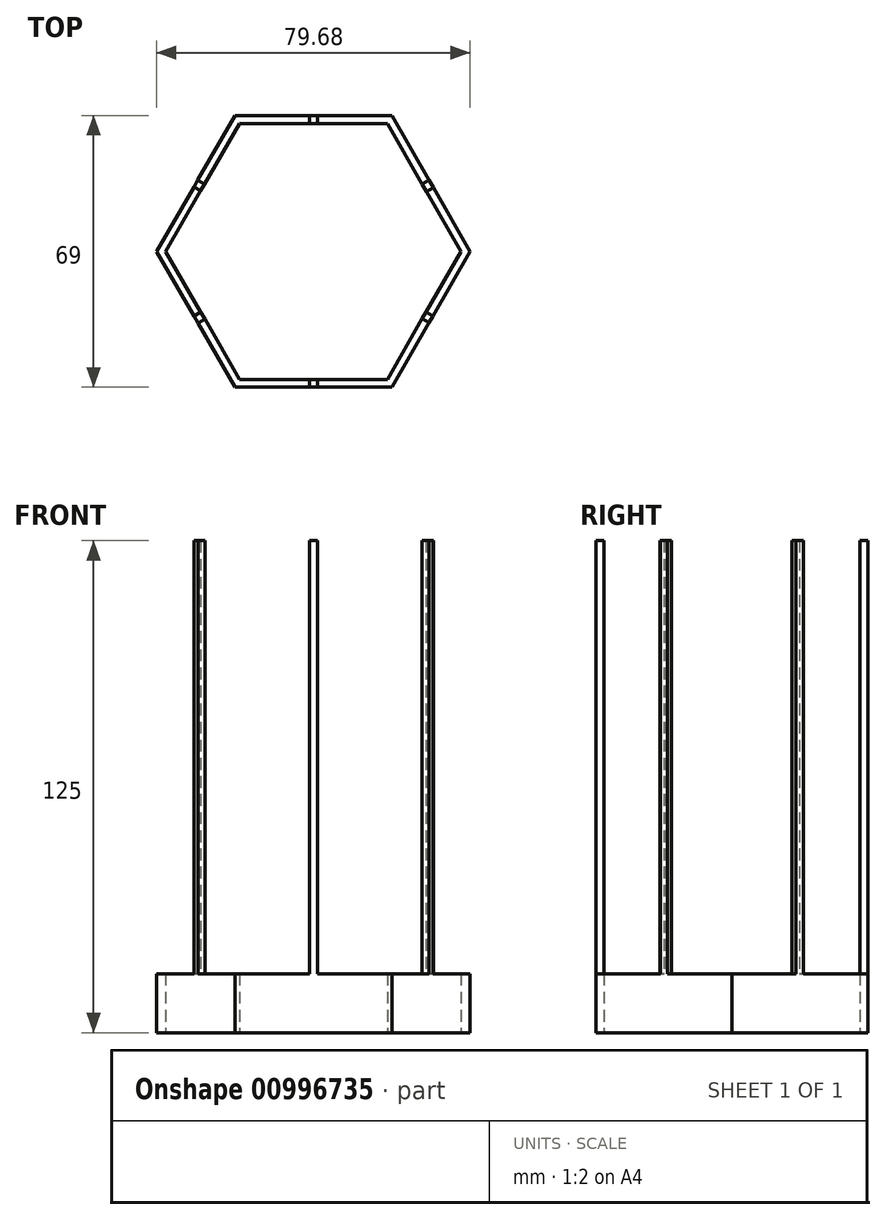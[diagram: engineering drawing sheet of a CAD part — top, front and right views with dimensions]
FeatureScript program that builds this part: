
annotation { "Feature Type Name" : "Feature", "Feature Type Description" : "" }
export const myFeature = defineFeature(function(context is Context, id is Id, definition is map)
    precondition{}
    {
        {
            var Q0;
            Q0=qCreatedBy(makeId("Top.planeOp"),FACE);
            var sketch = newSketch(context, id + "F0", { "sketchPlane" : qUnion([Q0])});
            skCircle(sketch, "E0.cCircle", {"center": v(0, 0) * mm, "radius": 34.5 * mm, "construction": true});
            skLineSegment(sketch, "E0.0", {"start": v(19.92, -34.5) * mm, "end": v(-19.92, -34.5) * mm});
            skLineSegment(sketch, "E0.1", {"start": v(-19.92, -34.5) * mm, "end": v(-39.84, 0) * mm});
            skLineSegment(sketch, "E0.2", {"start": v(-39.84, 0) * mm, "end": v(-19.92, 34.5) * mm});
            skLineSegment(sketch, "E0.3", {"start": v(-19.92, 34.5) * mm, "end": v(19.92, 34.5) * mm});
            skLineSegment(sketch, "E0.4", {"start": v(19.92, 34.5) * mm, "end": v(39.84, 0) * mm});
            skLineSegment(sketch, "E0.5", {"start": v(39.84, 0) * mm, "end": v(19.92, -34.5) * mm});
            skPoint(sketch, "E0.0.midPoint", {"position": v(0, -34.5) * mm});
            skCircle(sketch, "E1.cCircle", {"center": v(0, 0) * mm, "radius": 32.5 * mm, "construction": true});
            skLineSegment(sketch, "E1.0", {"start": v(18.76, -32.5) * mm, "end": v(-18.76, -32.5) * mm});
            skLineSegment(sketch, "E1.1", {"start": v(-18.76, -32.5) * mm, "end": v(-37.53, 0) * mm});
            skLineSegment(sketch, "E1.2", {"start": v(-37.53, 0) * mm, "end": v(-18.76, 32.5) * mm});
            skLineSegment(sketch, "E1.3", {"start": v(-18.76, 32.5) * mm, "end": v(18.76, 32.5) * mm});
            skLineSegment(sketch, "E1.4", {"start": v(18.76, 32.5) * mm, "end": v(37.53, 0) * mm});
            skLineSegment(sketch, "E1.5", {"start": v(37.53, 0) * mm, "end": v(18.76, -32.5) * mm});
            skPoint(sketch, "E1.0.midPoint", {"position": v(0, -32.5) * mm});
            skSolve(sketch);
        }
        {
            var Q0;
            Q0=makeQuery(id+"F0.imprint","IMPRINT",FACE,{"disambiguationData":[TD([[makeQuery(id+"F0.imprint","IMPRINT",EDGE,{"derivedFrom":sQuery(id+"F0.wireOp",EDGE,"E0.0")}),-1.0]])]});
            extrude(context, id + "F1", {"entities" : qUnion([Q0]), "depth" : 15 * mm, "offsetDistance" : 25 * mm});
        }
        {
            var Q0;
            Q0=makeQuery(id+"F1.opExtrude","CAP_FACE",FACE,{"disambiguationData":[OSD([sQuery(id+"F0.wireOp",EDGE,"E0.0"),sQuery(id+"F0.wireOp",EDGE,"E0.1"),sQuery(id+"F0.wireOp",EDGE,"E0.2"),sQuery(id+"F0.wireOp",EDGE,"E0.3"),sQuery(id+"F0.wireOp",EDGE,"E0.4"),sQuery(id+"F0.wireOp",EDGE,"E0.5"),sQuery(id+"F0.wireOp",EDGE,"E1.0"),sQuery(id+"F0.wireOp",EDGE,"E1.1"),sQuery(id+"F0.wireOp",EDGE,"E1.2"),sQuery(id+"F0.wireOp",EDGE,"E1.3"),sQuery(id+"F0.wireOp",EDGE,"E1.4"),sQuery(id+"F0.wireOp",EDGE,"E1.5")])],"isStart":false});
            var sketch = newSketch(context, id + "F2", { "sketchPlane" : qUnion([Q0])});
            skLineSegment(sketch, "E2", {"start": v(0, -34.5) * mm, "end": v(0, 34.5) * mm});
            skLineSegment(sketch, "E3", {"start": v(0, 34.5) * mm, "end": v(1, 34.5) * mm});
            skLineSegment(sketch, "E4", {"start": v(1, 34.5) * mm, "end": v(1, -34.5) * mm});
            skLineSegment(sketch, "E5", {"start": v(-1, -34.5) * mm, "end": v(-1, 34.5) * mm});
            skLineSegment(sketch, "E6", {"start": v(-29.88, 17.25) * mm, "end": v(29.88, -17.25) * mm});
            skLineSegment(sketch, "E7", {"start": v(-30.38, 16.38) * mm, "end": v(29.38, -18.12) * mm});
            skLineSegment(sketch, "E8", {"start": v(-29.38, 18.12) * mm, "end": v(30.38, -16.38) * mm});
            skLineSegment(sketch, "E9", {"start": v(29.88, 17.25) * mm, "end": v(-29.88, -17.25) * mm});
            skLineSegment(sketch, "E10", {"start": v(-30.38, -16.38) * mm, "end": v(29.38, 18.12) * mm});
            skLineSegment(sketch, "E11", {"start": v(30.46, 16.25) * mm, "end": v(-29.3, -18.25) * mm});
            skPoint(sketch, "E11.startSnap0", {"position": v(28.15, 16.25) * mm});
            skSolve(sketch);
        }
        {
            var Q0;
            {var subQ0=sQuery(id+"F2.wireOp",EDGE,"E6");var subQ1=makeQuery(id+"F1.opExtrude","CAP_EDGE",EDGE,{"disambiguationData":[OSD([sQuery(id+"F0.wireOp",EDGE,"E0.2")])],"isStart":false});var subQ2=makeQuery(id+"F2.imprint","INTERSECT",VERTEX,{"derivedFrom":[subQ1,subQ0]});Q0=makeQuery(id+"F2.imprint","IMPRINT",FACE,{"disambiguationData":[TD([[makeQuery(id+"F2.imprint","IMPRINT",EDGE,{"disambiguationData":[TD([[subQ2,-1.0]])],"derivedFrom":subQ0}),-1.0]])]});}
            var Q1;
            {var subQ0=sQuery(id+"F2.wireOp",EDGE,"E6");var subQ1=makeQuery(id+"F1.opExtrude","CAP_EDGE",EDGE,{"disambiguationData":[OSD([sQuery(id+"F0.wireOp",EDGE,"E0.2")])],"isStart":false});var subQ2=makeQuery(id+"F2.imprint","INTERSECT",VERTEX,{"derivedFrom":[subQ1,subQ0]});Q1=makeQuery(id+"F2.imprint","IMPRINT",FACE,{"disambiguationData":[TD([[makeQuery(id+"F2.imprint","IMPRINT",EDGE,{"disambiguationData":[TD([[subQ2,-1.0]])],"derivedFrom":subQ0}),1.0]])]});}
            var Q2;
            {var subQ1=makeQuery(id+"F1.opExtrude","CAP_EDGE",EDGE,{"disambiguationData":[OSD([sQuery(id+"F0.wireOp",EDGE,"E0.3")])],"isStart":false});var subQ5=sQuery(id+"F2.wireOp",EDGE,"E5");var subQ6=makeQuery(id+"F2.imprint","INTERSECT",VERTEX,{"derivedFrom":[subQ1,subQ5]});Q2=makeQuery(id+"F2.imprint","IMPRINT",FACE,{"disambiguationData":[TD([[makeQuery(id+"F2.imprint","IMPRINT",EDGE,{"disambiguationData":[TD([[subQ6,1.0]])],"derivedFrom":subQ5}),-1.0]])]});}
            var Q3;
            {var subQ0=sQuery(id+"F2.wireOp",EDGE,"E3");Q3=makeQuery(id+"F2.imprint","IMPRINT",FACE,{"disambiguationData":[TD([[makeQuery(id+"F2.imprint","IMPRINT",EDGE,{"derivedFrom":subQ0}),-1.0]])]});}
            var Q4;
            {var subQ0=sQuery(id+"F2.wireOp",EDGE,"E9");var subQ1=makeQuery(id+"F1.opExtrude","CAP_EDGE",EDGE,{"disambiguationData":[OSD([sQuery(id+"F0.wireOp",EDGE,"E0.4")])],"isStart":false});var subQ2=makeQuery(id+"F2.imprint","INTERSECT",VERTEX,{"derivedFrom":[subQ1,subQ0]});Q4=makeQuery(id+"F2.imprint","IMPRINT",FACE,{"disambiguationData":[TD([[makeQuery(id+"F2.imprint","IMPRINT",EDGE,{"disambiguationData":[TD([[subQ2,-1.0]])],"derivedFrom":subQ0}),-1.0]])]});}
            var Q5;
            {var subQ0=sQuery(id+"F2.wireOp",EDGE,"E9");var subQ1=makeQuery(id+"F1.opExtrude","CAP_EDGE",EDGE,{"disambiguationData":[OSD([sQuery(id+"F0.wireOp",EDGE,"E0.4")])],"isStart":false});var subQ2=makeQuery(id+"F2.imprint","INTERSECT",VERTEX,{"derivedFrom":[subQ1,subQ0]});Q5=makeQuery(id+"F2.imprint","IMPRINT",FACE,{"disambiguationData":[TD([[makeQuery(id+"F2.imprint","IMPRINT",EDGE,{"disambiguationData":[TD([[subQ2,-1.0]])],"derivedFrom":subQ0}),1.0]])]});}
            var Q6;
            {var subQ0=sQuery(id+"F2.wireOp",EDGE,"E6");var subQ1=makeQuery(id+"F1.opExtrude","CAP_EDGE",EDGE,{"disambiguationData":[OSD([sQuery(id+"F0.wireOp",EDGE,"E0.5")])],"isStart":false});var subQ2=makeQuery(id+"F2.imprint","INTERSECT",VERTEX,{"derivedFrom":[subQ1,subQ0]});Q6=makeQuery(id+"F2.imprint","IMPRINT",FACE,{"disambiguationData":[TD([[makeQuery(id+"F2.imprint","IMPRINT",EDGE,{"disambiguationData":[TD([[subQ2,1.0]])],"derivedFrom":subQ0}),1.0]])]});}
            var Q7;
            {var subQ0=sQuery(id+"F2.wireOp",EDGE,"E6");var subQ1=makeQuery(id+"F1.opExtrude","CAP_EDGE",EDGE,{"disambiguationData":[OSD([sQuery(id+"F0.wireOp",EDGE,"E0.5")])],"isStart":false});var subQ2=makeQuery(id+"F2.imprint","INTERSECT",VERTEX,{"derivedFrom":[subQ1,subQ0]});Q7=makeQuery(id+"F2.imprint","IMPRINT",FACE,{"disambiguationData":[TD([[makeQuery(id+"F2.imprint","IMPRINT",EDGE,{"disambiguationData":[TD([[subQ2,1.0]])],"derivedFrom":subQ0}),-1.0]])]});}
            var Q8;
            {var subQ0=sQuery(id+"F2.wireOp",EDGE,"E2");var subQ1=makeQuery(id+"F1.opExtrude","CAP_EDGE",EDGE,{"disambiguationData":[OSD([sQuery(id+"F0.wireOp",EDGE,"E0.0")])],"isStart":false});var subQ2=makeQuery(id+"F2.imprint","INTERSECT",VERTEX,{"derivedFrom":[subQ1,subQ0]});Q8=makeQuery(id+"F2.imprint","IMPRINT",FACE,{"disambiguationData":[TD([[makeQuery(id+"F2.imprint","IMPRINT",EDGE,{"disambiguationData":[TD([[subQ2,-1.0]])],"derivedFrom":subQ0}),-1.0]])]});}
            var Q9;
            {var subQ0=sQuery(id+"F2.wireOp",EDGE,"E2");var subQ1=makeQuery(id+"F1.opExtrude","CAP_EDGE",EDGE,{"disambiguationData":[OSD([sQuery(id+"F0.wireOp",EDGE,"E0.0")])],"isStart":false});var subQ2=makeQuery(id+"F2.imprint","INTERSECT",VERTEX,{"derivedFrom":[subQ1,subQ0]});Q9=makeQuery(id+"F2.imprint","IMPRINT",FACE,{"disambiguationData":[TD([[makeQuery(id+"F2.imprint","IMPRINT",EDGE,{"disambiguationData":[TD([[subQ2,-1.0]])],"derivedFrom":subQ0}),1.0]])]});}
            var Q10;
            {var subQ0=sQuery(id+"F2.wireOp",EDGE,"E9");var subQ1=makeQuery(id+"F1.opExtrude","CAP_EDGE",EDGE,{"disambiguationData":[OSD([sQuery(id+"F0.wireOp",EDGE,"E0.1")])],"isStart":false});var subQ2=makeQuery(id+"F2.imprint","INTERSECT",VERTEX,{"derivedFrom":[subQ1,subQ0]});Q10=makeQuery(id+"F2.imprint","IMPRINT",FACE,{"disambiguationData":[TD([[makeQuery(id+"F2.imprint","IMPRINT",EDGE,{"disambiguationData":[TD([[subQ2,1.0]])],"derivedFrom":subQ0}),1.0]])]});}
            var Q11;
            {var subQ0=sQuery(id+"F2.wireOp",EDGE,"E9");var subQ1=makeQuery(id+"F1.opExtrude","CAP_EDGE",EDGE,{"disambiguationData":[OSD([sQuery(id+"F0.wireOp",EDGE,"E0.1")])],"isStart":false});var subQ2=makeQuery(id+"F2.imprint","INTERSECT",VERTEX,{"derivedFrom":[subQ1,subQ0]});Q11=makeQuery(id+"F2.imprint","IMPRINT",FACE,{"disambiguationData":[TD([[makeQuery(id+"F2.imprint","IMPRINT",EDGE,{"disambiguationData":[TD([[subQ2,1.0]])],"derivedFrom":subQ0}),-1.0]])]});}
            extrude(context, id + "F3", {"entities" : qUnion([Q0, Q1, Q2, Q3, Q4, Q5, Q6, Q7, Q8, Q9, Q10, Q11]), "operationType" : NewBodyOperationType.ADD, "depth" : 110 * mm, "offsetDistance" : 25 * mm});
        }
        {
            var Q0;
            {var subQ0=sQuery(id+"F0.wireOp",EDGE,"E0.3");Q0=makeQuery(id+"F3.boolean.opBoolean","MERGE",FACE,{"derivedFrom":[makeQuery(id+"F1.opExtrude","SWEPT_FACE",FACE,{"disambiguationData":[OSD([subQ0])]}),makeQuery(id+"F3.opExtrude","SWEPT_FACE",FACE,{"disambiguationData":[OSD([subQ0,sQuery(id+"F2.wireOp",EDGE,"E3")])]})]});}
            var sketch = newSketch(context, id + "F4", { "sketchPlane" : qUnion([Q0])});
            skLineSegment(sketch, "E12.bottom", {"start": v(-1, 37) * mm, "end": v(1, 37) * mm});
            skLineSegment(sketch, "E12.top", {"start": v(-1, 35) * mm, "end": v(1, 35) * mm});
            skLineSegment(sketch, "E12.left", {"start": v(-1, 37) * mm, "end": v(-1, 35) * mm});
            skLineSegment(sketch, "E12.right", {"start": v(1, 37) * mm, "end": v(1, 35) * mm});
            skSolve(sketch);
        }
        {
            var Q0;
            Q0=makeQuery(id+"F4.imprint","IMPRINT",FACE,{"disambiguationData":[TD([[makeQuery(id+"F4.imprint","IMPRINT",EDGE,{"derivedFrom":sQuery(id+"F4.wireOp",EDGE,"E12.bottom")}),-1.0]])]});
            extrude(context, id + "F5", {"entities" : qUnion([Q0]), "operationType" : NewBodyOperationType.ADD, "oppositeDirection" : true, "depth" : 2 * mm, "offsetDistance" : 25 * mm});
        }
    });
